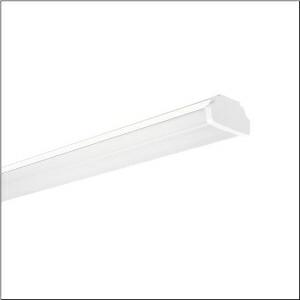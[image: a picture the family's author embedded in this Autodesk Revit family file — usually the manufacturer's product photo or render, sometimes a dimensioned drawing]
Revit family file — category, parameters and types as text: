
# Revit family: modario_r__31_mo_53bm812c1v6075_d0f6
name_source: partatom
category: Lighting Fixtures
units: mm (PartAtom-declared; Revit-internal decimal feet)

## family parameters
Cut with Voids When Loaded = No
Host = Face
Light Source = No
Part Type = Normal
Room Calculation Point = No
Round Connector Dimension = Use Diameter
Shared = No

## types (1)
- --- (1 x LED, 7640 lm, 48.9 W, 6500K)
    Apparent Load = 49 VA
    CIE Flux Codes = 47 80 95 92 100
    Color Rendering = 80
    Color Temperature = 6500K
    Default Elevation = 1800 mm
    Description = Modario® 31 MOluminaire insert, length: 1.495mm, width: 81mm, height: 82mm, LED rated luminous flux: 7.640lm, light colour: 865, control gear: ON/OFF Multilumen, CLOi, control gear: ECG Multilumen, with plug, 3-pole, with phase selection, mains connection: 220..240V, AC, 50/60Hz, primary optical cover: cover, of PMMA, light emission: direct distribution, primary light characteristic: symmetric, protection rating (complete): IP20, protection rating (LED compartment): IP50, insulation class (complete): insulation class I (protective earthing), certification: CE, ENEC, VDE, UKCA, permissible ambient temperature for indoor applications: -35..+30°C, corresponds to IFS (International Featured Standards) requirements for safety and quality in the food industry, reducing of maximum allowable ambient temperature of 5°C with ceiling mounting, packaging unit: 1 piece
    Height = 92 mm
    Lamp = 1 x LED
    Lamp Light Flux = 7640 lm
    Lamp Power = 48.9 W
    Lamp count = 1
    Length = 1495 mm
    Luminous efficacy = 156 lm/W
    Manufacturer = Siteco
    ModVariant = No
    Model = 53BM812C1V6075
    Mounting Place = Ceiling
    Mounting Type = Pendant
    Number of Poles = 1
    OnlyDefault = Yes
    Power Factor = 1
    Product Name = Modario® 31 MO
    Product group = luminaire insert
    ProductGroupID = 902
    Protection Class = Protection class I
    Protection Degree = IP 20
    RLX_Detail_Level = 1
    RlxData = <blob elided: 40021 chars, md5=4bfe72d1>
    Socket = socket
    Standby Power = 0 W
    System Light Flux = 7640 lm
    System Power = 49 W
    Type Comments = factory setting: luminous flux: 100 % | (A | C | E) | 107 mA
    Type Image = l_1003447.jpg
    URL = http://relux.com
    VarID = @adj_131349
    Voltage = 0 V
    Weight = 0.00 kg
    Width = 81 mm

## geometry (parser evidence)
native form markers: Blend x4, Sweep x12
no freeform markers — native parametric forms only
